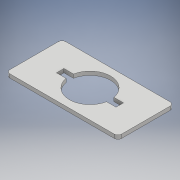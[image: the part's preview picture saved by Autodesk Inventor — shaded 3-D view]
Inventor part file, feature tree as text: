
AUTODESK INVENTOR PART (.ipt)
format: ipt  version: 2017 (Build 210142000, 142)  size: 118,784 bytes
history: native  units: mm
features: extrude x1, fillet x1, sketch x1
ambient origin geometry x8: Origin, YZ Plane, XZ Plane, XY Plane, X Axis, Y Axis, Z Axis, Center Point
bodies: Solid1 (feature_tree)
feature tree (3):
  extrude  "Extrusion1"  Depth=32.0mm
  fillet  "Fillet1"  Radius=4.0mm
  sketch  "Sketch1"  dims[d0=22.1mm d1=32.0mm d2=4.0mm d3=60.0mm d4=30.0mm d5=2.0mm d6=0.0mm d7=2.0mm]
